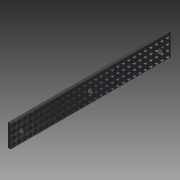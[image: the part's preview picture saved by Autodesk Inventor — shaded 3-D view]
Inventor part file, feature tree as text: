
AUTODESK INVENTOR PART (.ipt)
format: ipt  version: 2015 SP1 (Build 190203100, 203)  size: 396,800 bytes
history: native  units: in
note: dims shown in document units (in); Inventor stores cm internally (conversion verified against a paired STEP export)
features: sketch x3, extrude x2, pattern_linear x1, hole x1
ambient origin geometry x8: Origin, YZ Plane, XZ Plane, XY Plane, X Axis, Y Axis, Z Axis, Center Point
bodies: Solid1 (feature_tree)
feature tree (7):
  extrude  "Extrusion1"  Depth=7.25in
  extrude  "Extrusion2"  Depth=0.125in
  pattern_linear  "Rectangular Pattern1"  Spacing1=0.125in  [1 undecoded]
  hole  "Hole1"  [1 undecoded]
  sketch  "Sketch1"  dims[d0=1.0in d1=7.25in]
  sketch  "Sketch2"  dims[d2=0.125in d3=0.0in d4=0.125in]
  sketch  "Sketch3"  dims[d5=1.0in d6=0.125in d7=1.0in d8=135.0deg d9=45.0deg d10=90.0deg d11=135.0deg d12=90.0deg d13=90.0deg d14=0.0625in d15=-0.4123in d16=11.4173in d18=0.25in d19=0.5in d20=0.5in d21=0.5in d22=3.625in d23=0.5in d24=0.5in d25=0.25in d26=0.75in d27=0.375in d28=0.25in d29=0.5635in d30=1.0in d31=0.8108in]
note: 2 required parameter values undecoded (feature->parameter linkage not recoverable at this tier; creation-order binding heuristic only, values carry confidence <= 0.55)
